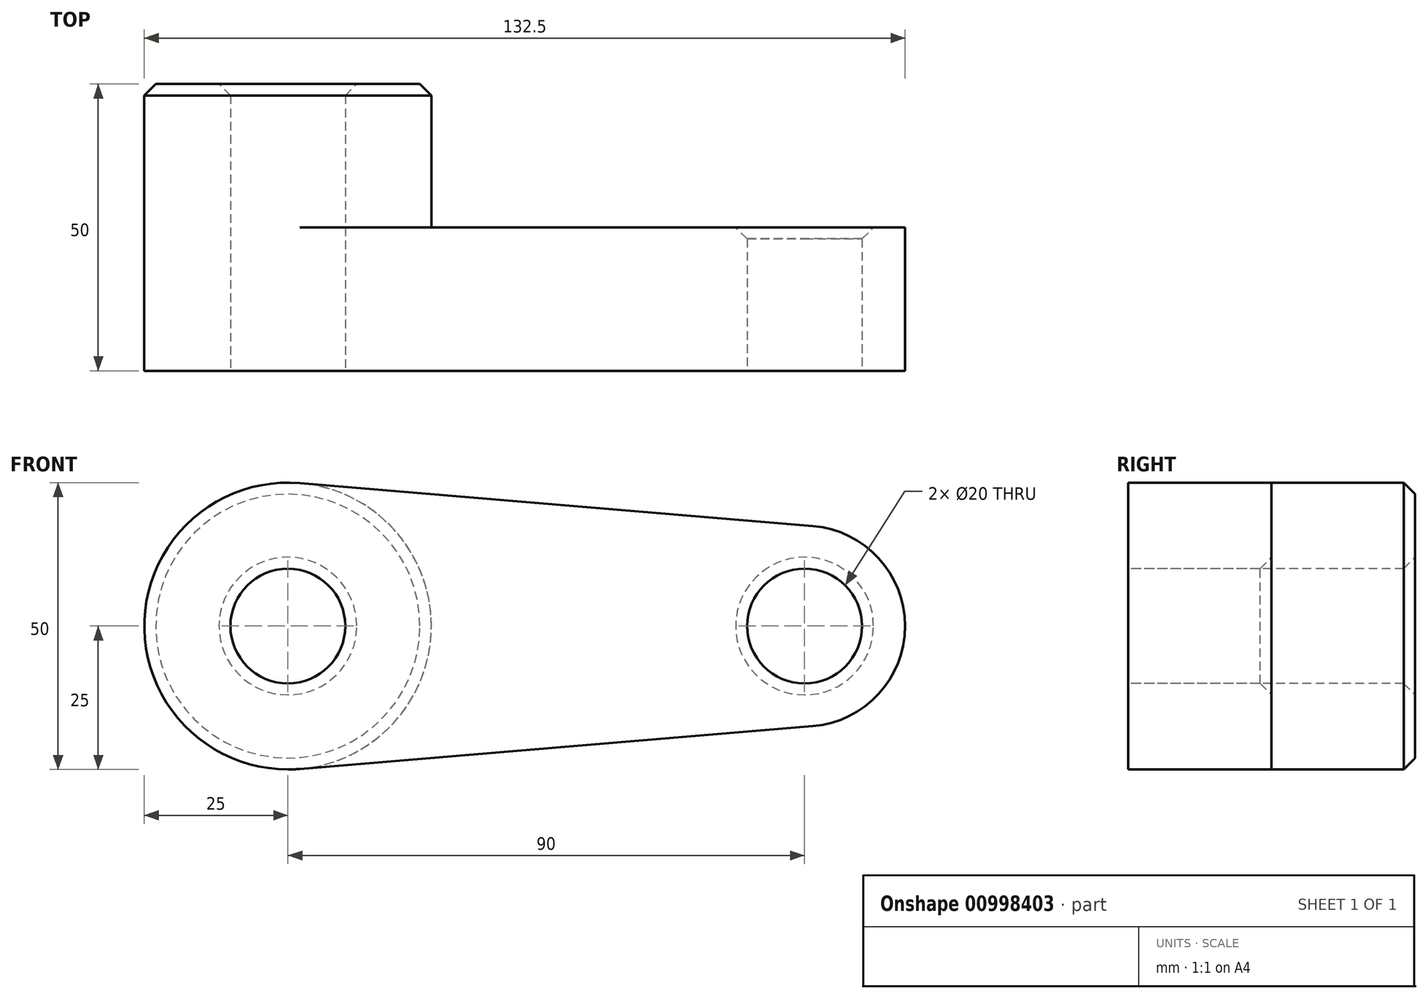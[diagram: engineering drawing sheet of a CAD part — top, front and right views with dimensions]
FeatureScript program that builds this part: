
annotation { "Feature Type Name" : "Feature", "Feature Type Description" : "" }
export const myFeature = defineFeature(function(context is Context, id is Id, definition is map)
    precondition{}
    {
        {
            var Q0;
            Q0=qCreatedBy(makeId("Front.planeOp"),FACE);
            var sketch = newSketch(context, id + "F0", { "sketchPlane" : qUnion([Q0])});
            skCircle(sketch, "E0", {"center": v(0, 0) * mm, "radius": 25 * mm});
            skCircle(sketch, "E1", {"center": v(90, 0) * mm, "radius": 17.5 * mm});
            skLineSegment(sketch, "E2", {"start": v(2.08, 24.91) * mm, "end": v(91.46, 17.44) * mm});
            skLineSegment(sketch, "E3", {"start": v(2.08, -24.91) * mm, "end": v(91.46, -17.44) * mm});
            skCircle(sketch, "E4", {"center": v(0, 0) * mm, "radius": 10 * mm});
            skCircle(sketch, "E5", {"center": v(90, 0) * mm, "radius": 10 * mm});
            skSolve(sketch);
        }
        {
            var Q0;
            Q0 = qSketchRegion(id + "F0", true);
            extrude(context, id + "F1", {"entities" : qUnion([Q0]), "oppositeDirection" : true, "depth" : 25 * mm, "offsetDistance" : 25 * mm});
        }
        {
            var Q0;
            Q0=makeQuery(id+"F0.imprint","IMPRINT",FACE,{"disambiguationData":[TD([[makeQuery(id+"F0.imprint","IMPRINT",EDGE,{"derivedFrom":sQuery(id+"F0.wireOp",EDGE,"E4")}),-1.0]])]});
            extrude(context, id + "F2", {"entities" : qUnion([Q0]), "operationType" : NewBodyOperationType.ADD, "oppositeDirection" : true, "depth" : 50 * mm, "offsetDistance" : 25 * mm});
        }
        {
            var Q0;
            Q0=makeQuery(id+"F2.opExtrude","CAP_EDGE",EDGE,{"disambiguationData":[OSD([sQuery(id+"F0.wireOp",EDGE,"E4")])],"isStart":false});
            var Q1;
            Q1=makeQuery(id+"F1.opExtrude","CAP_EDGE",EDGE,{"disambiguationData":[OSD([sQuery(id+"F0.wireOp",EDGE,"E5")])],"isStart":false});
            var Q2;
            Q2=makeQuery(id+"F2.opExtrude","CAP_EDGE",EDGE,{"disambiguationData":[OSD([sQuery(id+"F0.wireOp",EDGE,"E0")])],"isStart":false});
            chamfer(context, id + "F3", {"entities" : qUnion([Q0, Q1, Q2]), "width" : 2 * mm, "tangentPropagation" : true});
        }
    });
